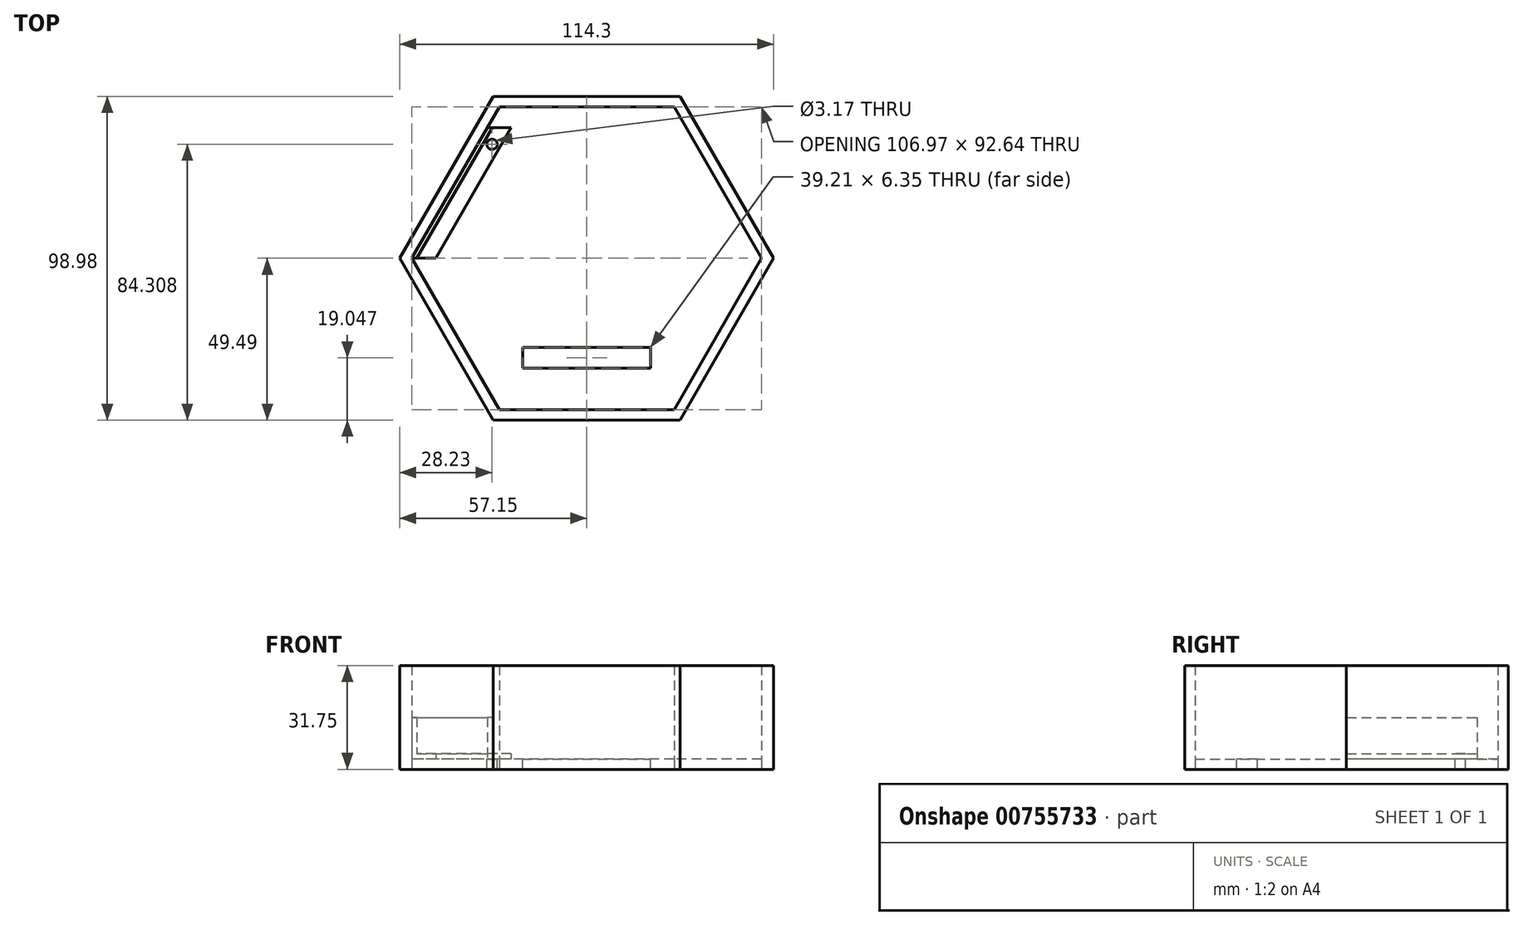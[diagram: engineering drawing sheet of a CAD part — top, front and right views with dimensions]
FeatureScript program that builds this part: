
annotation { "Feature Type Name" : "Feature", "Feature Type Description" : "" }
export const myFeature = defineFeature(function(context is Context, id is Id, definition is map)
    precondition{}
    {
        {
            var Q0;
            Q0=qCreatedBy(makeId("Top.planeOp"),FACE);
            var sketch = newSketch(context, id + "F0", { "sketchPlane" : qUnion([Q0])});
            skCircle(sketch, "E0.cCircle", {"center": v(0, 0) * mm, "radius": 57.15 * mm, "construction": true});
            skLineSegment(sketch, "E0.0", {"start": v(-28.58, 49.5) * mm, "end": v(28.58, 49.5) * mm});
            skLineSegment(sketch, "E0.1", {"start": v(28.57, 49.5) * mm, "end": v(57.15, 0) * mm});
            skLineSegment(sketch, "E0.2", {"start": v(57.15, 0) * mm, "end": v(28.57, -49.5) * mm});
            skLineSegment(sketch, "E0.3", {"start": v(28.58, -49.5) * mm, "end": v(-28.57, -49.5) * mm});
            skLineSegment(sketch, "E0.4", {"start": v(-28.57, -49.5) * mm, "end": v(-57.15, 0) * mm});
            skLineSegment(sketch, "E0.5", {"start": v(-57.15, 0) * mm, "end": v(-28.57, 49.5) * mm});
            skCircle(sketch, "E1.cCircle", {"center": v(0, 0) * mm, "radius": 53.48 * mm, "construction": true});
            skLineSegment(sketch, "E1.0", {"start": v(-53.48, 0) * mm, "end": v(-26.74, 46.32) * mm});
            skLineSegment(sketch, "E1.1", {"start": v(-26.74, 46.32) * mm, "end": v(26.74, 46.32) * mm});
            skLineSegment(sketch, "E1.2", {"start": v(26.74, 46.32) * mm, "end": v(53.48, 0) * mm});
            skLineSegment(sketch, "E1.3", {"start": v(53.48, 0) * mm, "end": v(26.74, -46.32) * mm});
            skLineSegment(sketch, "E1.4", {"start": v(26.74, -46.32) * mm, "end": v(-26.74, -46.32) * mm});
            skLineSegment(sketch, "E1.5", {"start": v(-26.74, -46.32) * mm, "end": v(-53.48, 0) * mm});
            skSolve(sketch);
        }
        {
            var Q0;
            Q0=makeQuery(id+"F0.imprint","IMPRINT",FACE,{"disambiguationData":[TD([[makeQuery(id+"F0.imprint","IMPRINT",EDGE,{"derivedFrom":sQuery(id+"F0.wireOp",EDGE,"E1.0")}),-1.0]])]});
            extrude(context, id + "F1", {"entities" : qUnion([Q0]), "depth" : 3.17 * mm, "offsetDistance" : 25.4 * mm});
        }
        {
            var Q0;
            Q0=makeQuery(id+"F1.opExtrude","CAP_FACE",FACE,{"disambiguationData":[OSD([sQuery(id+"F0.wireOp",EDGE,"E1.0"),sQuery(id+"F0.wireOp",EDGE,"E1.1"),sQuery(id+"F0.wireOp",EDGE,"E1.2"),sQuery(id+"F0.wireOp",EDGE,"E1.3"),sQuery(id+"F0.wireOp",EDGE,"E1.4"),sQuery(id+"F0.wireOp",EDGE,"E1.5")])],"isStart":false});
            var sketch = newSketch(context, id + "F2", { "sketchPlane" : qUnion([Q0])});
            skLineSegment(sketch, "E2.bottom", {"start": v(-19.6, -27.27) * mm, "end": v(19.6, -27.27) * mm});
            skLineSegment(sketch, "E2.top", {"start": v(-19.6, -33.62) * mm, "end": v(19.6, -33.62) * mm});
            skLineSegment(sketch, "E2.left", {"start": v(-19.6, -27.27) * mm, "end": v(-19.6, -33.62) * mm});
            skLineSegment(sketch, "E2.right", {"start": v(19.6, -27.27) * mm, "end": v(19.6, -33.62) * mm});
            skPoint(sketch, "E2.middle", {"position": v(0, -30.44) * mm});
            skSolve(sketch);
        }
        {
            var Q0;
            Q0=makeQuery(id+"F2.imprint","IMPRINT",FACE,{"disambiguationData":[TD([[makeQuery(id+"F2.imprint","IMPRINT",EDGE,{"derivedFrom":sQuery(id+"F2.wireOp",EDGE,"E2.bottom")}),-1.0]])]});
            extrude(context, id + "F3", {"entities" : qUnion([Q0]), "operationType" : NewBodyOperationType.REMOVE, "oppositeDirection" : true, "depth" : 25.4 * mm, "offsetDistance" : 25.4 * mm});
        }
        {
            var Q0;
            Q0=makeQuery(id+"F0.imprint","IMPRINT",FACE,{"disambiguationData":[TD([[makeQuery(id+"F0.imprint","IMPRINT",EDGE,{"derivedFrom":sQuery(id+"F0.wireOp",EDGE,"E0.0")}),-1.0]])]});
            extrude(context, id + "F4", {"entities" : qUnion([Q0]), "depth" : 31.75 * mm, "offsetDistance" : 25.4 * mm});
        }
        {
            var Q0;
            Q0=makeQuery(id+"F1.opExtrude","CAP_FACE",FACE,{"disambiguationData":[OSD([sQuery(id+"F0.wireOp",EDGE,"E1.0"),sQuery(id+"F0.wireOp",EDGE,"E1.1"),sQuery(id+"F0.wireOp",EDGE,"E1.2"),sQuery(id+"F0.wireOp",EDGE,"E1.3"),sQuery(id+"F0.wireOp",EDGE,"E1.4"),sQuery(id+"F0.wireOp",EDGE,"E1.5")])],"isStart":false});
            var sketch = newSketch(context, id + "F5", { "sketchPlane" : qUnion([Q0])});
            skLineSegment(sketch, "E3", {"start": v(-23.08, 39.97) * mm, "end": v(-46.15, 0) * mm});
            skLineSegment(sketch, "E4", {"start": v(-23.08, 39.97) * mm, "end": v(-30.4, 39.97) * mm});
            skLineSegment(sketch, "E5", {"start": v(-46.15, 0) * mm, "end": v(-53.48, 0) * mm});
            skLineSegment(sketch, "E6", {"start": v(-51.9, 0) * mm, "end": v(-28.82, 39.97) * mm});
            skSolve(sketch);
        }
        {
            var Q0;
            {var subQ3=sQuery(id+"F5.wireOp",EDGE,"E6");Q0=makeQuery(id+"F5.imprint","IMPRINT",FACE,{"disambiguationData":[TD([[makeQuery(id+"F5.imprint","IMPRINT",EDGE,{"derivedFrom":subQ3}),1.0]])]});}
            extrude(context, id + "F6", {"entities" : qUnion([Q0]), "depth" : 12.7 * mm, "offsetDistance" : 25.4 * mm});
        }
        {
            var Q0;
            {var subQ0=sQuery(id+"F5.wireOp",EDGE,"E3");Q0=makeQuery(id+"F5.imprint","IMPRINT",FACE,{"disambiguationData":[TD([[makeQuery(id+"F5.imprint","IMPRINT",EDGE,{"derivedFrom":subQ0}),-1.0]])]});}
            extrude(context, id + "F7", {"entities" : qUnion([Q0]), "operationType" : NewBodyOperationType.ADD, "depth" : 1.59 * mm, "offsetDistance" : 25.4 * mm});
        }
        {
            var Q0;
            Q0=makeQuery(id+"F7.opExtrude","CAP_FACE",FACE,{"disambiguationData":[OSD([sQuery(id+"F5.wireOp",EDGE,"E3"),sQuery(id+"F5.wireOp",EDGE,"E4"),sQuery(id+"F5.wireOp",EDGE,"E5"),sQuery(id+"F5.wireOp",EDGE,"E6")])],"isStart":false});
            var sketch = newSketch(context, id + "F8", { "sketchPlane" : qUnion([Q0])});
            skCircle(sketch, "E7", {"center": v(-28.92, 34.82) * mm, "radius": 1.59 * mm});
            skLineSegment(sketch, "E8", {"start": v(-28.82, 39.97) * mm, "end": v(-23.08, 39.97) * mm});
            skLineSegment(sketch, "E9", {"start": v(-23.08, 39.97) * mm, "end": v(-34.61, 19.98) * mm});
            skSolve(sketch);
        }
        {
            var Q0;
            Q0=makeQuery(id+"F8.imprint","IMPRINT",FACE,{"disambiguationData":[TD([[makeQuery(id+"F8.imprint","IMPRINT",EDGE,{"derivedFrom":sQuery(id+"F8.wireOp",EDGE,"E7")}),1.0]])]});
            extrude(context, id + "F9", {"entities" : qUnion([Q0]), "operationType" : NewBodyOperationType.REMOVE, "oppositeDirection" : true, "depth" : 25.4 * mm, "offsetDistance" : 25.4 * mm});
        }
    });
